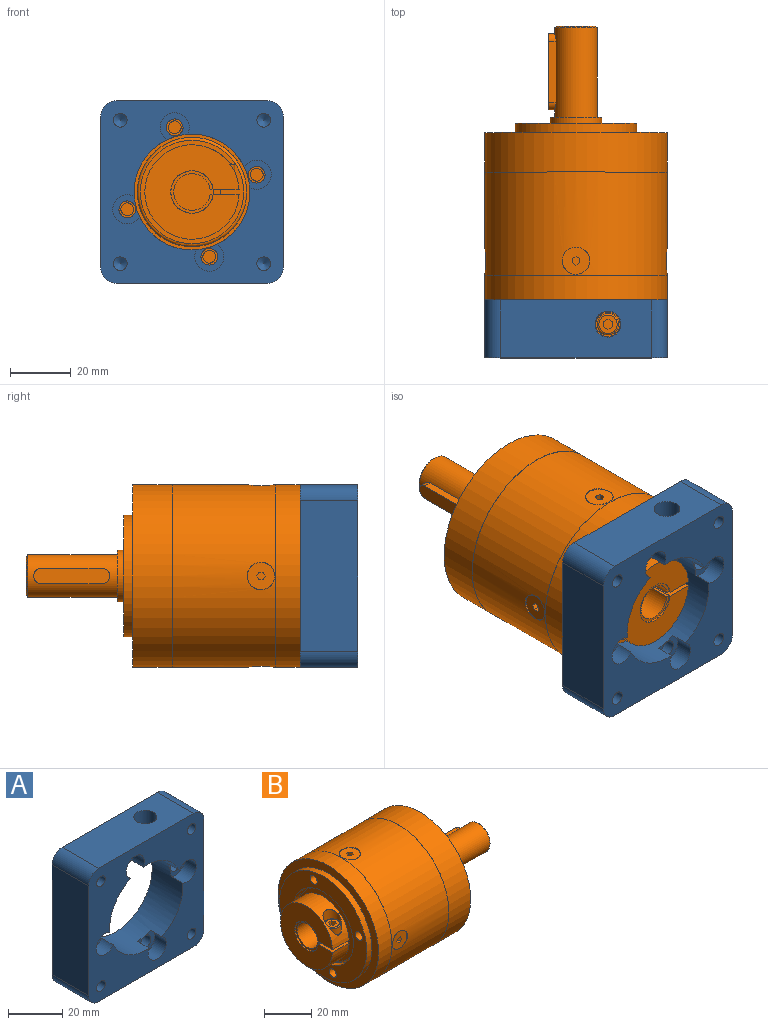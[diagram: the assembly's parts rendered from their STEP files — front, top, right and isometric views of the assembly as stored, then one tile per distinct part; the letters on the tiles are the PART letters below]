
ASSEMBLY  parts=2 mates=1
PART A: 34 faces, bbox 60x19x60 mm
  f0: plane 60x60mm, normal (0,-1,0), area 2122.8mm2, adj f1,f3,f4,f5,f6,f9,f11,f13
  f1: plane 49.4x19mm, normal (0,0,-1), area 938.6mm2, adj f0,f2,f32,f33
  f2: plane 60x60mm, normal (0,1,0), area 1452.2mm2, adj f1,f3,f4,f5,f16,f30,f31,f32
  f3: plane 49.4x19mm, normal (0,0,1), area 881.9mm2, adj f0,f2,f7,f30,f31
  f4: plane 49.4x19mm, normal (1,0,0), area 938.6mm2, adj f0,f2,f31,f32
  f5: plane 49.4x19mm, normal (-1,0,0), area 938.6mm2, adj f0,f2,f30,f33
  f6: cylinder r=19.05mm len=38.1mm, axis (0,-1,0), area 1679mm2, adj f0,f7,f17,f18,f19,f21,f22,f24
  f7: cylinder r=4.25mm len=17.94mm, axis (0,0,1), area 388.1mm2, adj f3,f6
  f8: cone r=0mm half-angle=59deg, axis (0,-1,0), area 18.6mm2, adj f9
  f9: cylinder r=2.25mm len=12mm, axis (0,-1,0), area 169.6mm2, adj f0,f8
  f10: cone r=0mm half-angle=59deg, axis (0,-1,0), area 18.6mm2, adj f11
  f11: cylinder r=2.25mm len=12mm, axis (0,-1,0), area 169.6mm2, adj f0,f10
  f12: cone r=0mm half-angle=59deg, axis (0,-1,0), area 18.6mm2, adj f13
  f13: cylinder r=2.25mm len=12mm, axis (0,-1,0), area 169.6mm2, adj f0,f12
  f14: cone r=0mm half-angle=59deg, axis (0,-1,0), area 18.6mm2, adj f15
  f15: cylinder r=2.25mm len=12mm, axis (0,-1,0), area 169.6mm2, adj f0,f14
  f16: cylinder r=26mm len=52mm, axis (0,1,0), area 490.1mm2, adj f2,f17
  f17: plane 52x52mm, normal (0,1,0), area 888.6mm2, adj f6,f16,f20,f23,f26,f29
  f18: plane 9.5x8.8mm, normal (0,-1,0), area 38.6mm2, adj f6,f19,f20
  f19: cylinder r=4.75mm len=9.5mm, axis (0,-1,0), area 132.7mm2, adj f0,f6,f18
  f20: cylinder r=2.75mm len=10mm, axis (0,-1,0), area 172.8mm2, adj f17,f18
  f21: plane 9.5x8.8mm, normal (0,-1,0), area 38.6mm2, adj f6,f22,f23
  f22: cylinder r=4.75mm len=9.5mm, axis (0,-1,0), area 132.7mm2, adj f0,f6,f21
  f23: cylinder r=2.75mm len=10mm, axis (0,-1,0), area 172.8mm2, adj f17,f21
  f24: plane 9.5x8.8mm, normal (0,-1,0), area 38.6mm2, adj f6,f25,f26
  f25: cylinder r=4.75mm len=9.5mm, axis (0,-1,0), area 132.7mm2, adj f0,f6,f24
  f26: cylinder r=2.75mm len=10mm, axis (0,-1,0), area 172.8mm2, adj f17,f24
  f27: plane 9.5x8.8mm, normal (0,-1,0), area 38.6mm2, adj f6,f28,f29
  f28: cylinder r=4.75mm len=9.5mm, axis (0,-1,0), area 132.7mm2, adj f0,f6,f27
  f29: cylinder r=2.75mm len=10mm, axis (0,-1,0), area 172.8mm2, adj f17,f27
  f30: cylinder r=5.3mm len=19mm, axis (0,-1,0), area 158.2mm2, adj f0,f2,f3,f5
  f31: cylinder r=5.3mm len=19mm, axis (0,-1,0), area 158.2mm2, adj f0,f2,f3,f4
  f32: cylinder r=5.3mm len=19mm, axis (0,-1,0), area 158.2mm2, adj f0,f1,f2,f4
  f33: cylinder r=5.3mm len=19mm, axis (0,-1,0), area 158.2mm2, adj f0,f1,f2,f5
PART B: 109 faces, bbox 103.2x60x60 mm
  f0: cylinder r=2.1mm len=4.5mm, axis (-1,0,0), area 59.4mm2, adj f2,f108
  f1: cylinder r=2.15mm len=8mm, axis (-1,0,0), area 108.1mm2, adj f2,f3
  f2: plane 4.3x4.3mm, normal (1,0,0), area 0.7mm2, adj f0,f1
  f3: cone r=2.65mm half-angle=45deg, axis (1,0,0), area 10.7mm2, adj f1,f4
  f4: cylinder r=2.65mm len=5.3mm, axis (-1,0,0), area 26.6mm2, adj f3,f5
  f5: torus R=8.66mm, axis (1,0,0), area 57.4mm2, adj f4,f6
  f6: plane 13x13mm, normal (1,0,0), area 81.2mm2, adj f5,f9
  f7: plane 25x5mm, normal (0,1,0), area 119.6mm2, adj f8,f10,f11,f12
  f8: plane 20x2.46mm, normal (0,0,-1), area 49.2mm2, adj f7,f10,f12,f13
  f9: cone r=7mm half-angle=45deg, axis (-1,0,0), area 30mm2, adj f6,f13
  f10: cylinder r=2.5mm len=5mm, axis (0,-1,0), area 17.5mm2, adj f7,f8,f11,f13
  f11: plane 20x2.46mm, normal (0,0,1), area 49.2mm2, adj f7,f10,f12,f13
  f12: cylinder r=2.5mm len=5mm, axis (0,-1,0), area 17.5mm2, adj f7,f8,f11,f13
  f13: cylinder r=7mm len=29.5mm, axis (-1,0,0), area 1182.4mm2, adj f8,f9,f10,f11,f12,f14
  f14: plane 17x17mm, normal (1,0,0), area 73mm2, adj f13,f15
  f15: cylinder r=8.5mm len=17mm, axis (-1,0,0), area 106.8mm2, adj f14,f21
  f16: plane 3x1.73mm, normal (0,-1,0), area 5.2mm2, adj f22,f23,f35,f67
  f17: plane 4.2x4.2mm, normal (1,0,0), area 13.9mm2, adj f25
  f18: plane 4.2x4.2mm, normal (1,0,0), area 13.9mm2, adj f26
  f19: plane 4.2x4.2mm, normal (1,0,0), area 13.9mm2, adj f27
  f20: plane 4.2x4.2mm, normal (1,0,0), area 13.9mm2, adj f28
  f21: plane 40x40mm, normal (1,0,0), area 1029.7mm2, adj f15,f29
  f22: plane 3x1.5mm, normal (-0.87,-0.5,0), area 5.2mm2, adj f16,f33,f35,f67
  f23: plane 3x1.5mm, normal (0.87,-0.5,0), area 5.2mm2, adj f16,f34,f35,f67
  f24: plane 2.89x2.5mm, normal (0,0,-1), area 5.4mm2, adj f36,f37,f38,f39,f40,f41
  f25: cylinder r=2.1mm len=8mm, axis (1,0,0), area 105.6mm2, adj f17,f42
  f26: cylinder r=2.1mm len=8mm, axis (1,0,0), area 105.6mm2, adj f18,f42
  f27: cylinder r=2.1mm len=8mm, axis (1,0,0), area 105.6mm2, adj f19,f42
  f28: cylinder r=2.1mm len=8mm, axis (1,0,0), area 105.6mm2, adj f20,f42
  f29: cylinder r=20mm len=40mm, axis (-1,0,0), area 377mm2, adj f21,f42
  f30: plane 2.89x2.5mm, normal (0,1,0), area 5.4mm2, adj f43,f44,f45,f46,f47,f48
  f31: plane 2.89x2.5mm, normal (0,-1,0), area 5.4mm2, adj f49,f50,f51,f52,f53,f54
  f32: plane 2.89x2.5mm, normal (0,0,1), area 5.4mm2, adj f55,f56,f57,f58,f59,f60
  f33: plane 3x1.5mm, normal (-0.87,0.5,0), area 5.2mm2, adj f22,f35,f61,f67
  f34: plane 3x1.5mm, normal (0.87,0.5,0), area 5.2mm2, adj f23,f35,f61,f67
  f35: plane 3.46x3mm, normal (0,0,1), area 7.8mm2, adj f16,f22,f23,f33,f34,f61
  f36: plane 2.5x1.44mm, normal (0,1,0), area 3.6mm2, adj f24,f37,f41,f62
  f37: plane 2.5x1.25mm, normal (0.87,0.5,0), area 3.6mm2, adj f24,f36,f38,f62
  f38: plane 2.5x1.25mm, normal (0.87,-0.5,0), area 3.6mm2, adj f24,f37,f39,f62
  f39: plane 2.5x1.44mm, normal (0,-1,0), area 3.6mm2, adj f24,f38,f40,f62
  f40: plane 2.5x1.25mm, normal (-0.87,-0.5,0), area 3.6mm2, adj f24,f39,f41,f62
  f41: plane 2.5x1.25mm, normal (-0.87,0.5,0), area 3.6mm2, adj f24,f36,f40,f62
  f42: plane 60x60mm, normal (1,0,0), area 1515.4mm2, adj f25,f26,f27,f28,f29,f63
  f43: plane 2.5x1.44mm, normal (0,0,1), area 3.6mm2, adj f30,f44,f48,f64
  f44: plane 2.5x1.25mm, normal (0.87,0,0.5), area 3.6mm2, adj f30,f43,f45,f64
  f45: plane 2.5x1.25mm, normal (0.87,0,-0.5), area 3.6mm2, adj f30,f44,f46,f64
  f46: plane 2.5x1.44mm, normal (0,0,-1), area 3.6mm2, adj f30,f45,f47,f64
  f47: plane 2.5x1.25mm, normal (-0.87,0,-0.5), area 3.6mm2, adj f30,f46,f48,f64
  f48: plane 2.5x1.25mm, normal (-0.87,0,0.5), area 3.6mm2, adj f30,f43,f47,f64
  f49: plane 2.5x1.44mm, normal (0,0,-1), area 3.6mm2, adj f31,f50,f54,f65
  f50: plane 2.5x1.25mm, normal (0.87,0,-0.5), area 3.6mm2, adj f31,f49,f51,f65
  f51: plane 2.5x1.25mm, normal (0.87,0,0.5), area 3.6mm2, adj f31,f50,f52,f65
  f52: plane 2.5x1.44mm, normal (0,0,1), area 3.6mm2, adj f31,f51,f53,f65
  f53: plane 2.5x1.25mm, normal (-0.87,0,0.5), area 3.6mm2, adj f31,f52,f54,f65
  f54: plane 2.5x1.25mm, normal (-0.87,0,-0.5), area 3.6mm2, adj f31,f49,f53,f65
  f55: plane 2.5x1.44mm, normal (0,-1,0), area 3.6mm2, adj f32,f56,f60,f66
  f56: plane 2.5x1.25mm, normal (0.87,-0.5,0), area 3.6mm2, adj f32,f55,f57,f66
  f57: plane 2.5x1.25mm, normal (0.87,0.5,0), area 3.6mm2, adj f32,f56,f58,f66
  f58: plane 2.5x1.44mm, normal (0,1,0), area 3.6mm2, adj f32,f57,f59,f66
  f59: plane 2.5x1.25mm, normal (-0.87,0.5,0), area 3.6mm2, adj f32,f58,f60,f66
  f60: plane 2.5x1.25mm, normal (-0.87,-0.5,0), area 3.6mm2, adj f32,f55,f59,f66
  f61: plane 3x1.73mm, normal (0,1,0), area 5.2mm2, adj f33,f34,f35,f67
  f62: plane 9x9mm, normal (0,0,-1), area 58.2mm2, adj f36,f37,f38,f39,f40,f41,f68
  f63: cylinder r=30mm len=60mm, axis (-1,0,0), area 2450.4mm2, adj f42,f69
  f64: plane 9x9mm, normal (0,1,0), area 58.2mm2, adj f43,f44,f45,f46,f47,f48,f70
  f65: plane 9x9mm, normal (0,-1,0), area 58.2mm2, adj f49,f50,f51,f52,f53,f54,f71
  f66: plane 9x9mm, normal (0,0,1), area 58.2mm2, adj f55,f56,f57,f58,f59,f60,f72
  f67: plane 6x6mm, normal (0,0,1), area 20.5mm2, adj f16,f22,f23,f33,f34,f61,f73
  f68: cylinder r=4.5mm len=9mm, axis (0,0,-1), area 6.5mm2, adj f62,f77
  f69: plane 60x60mm, normal (-1,0,0), area 9.4mm2, adj f63,f77
  f70: cylinder r=4.5mm len=9mm, axis (0,1,0), area 6.5mm2, adj f64,f77
  f71: cylinder r=4.5mm len=9mm, axis (0,-1,0), area 6.5mm2, adj f65,f77
  f72: cylinder r=4.5mm len=9mm, axis (0,0,1), area 6.5mm2, adj f66,f77
  f73: torus R=3mm, axis (0,0,1), area 16.4mm2, adj f67,f78
  f74: plane 19.5x0.96mm, normal (0,0,1), area 18.7mm2, adj f75,f79,f80,f83
  f75: plane 13.9x13.86mm, normal (-1,0,0), area 37.2mm2, adj f74,f76,f79,f80
  f76: plane 19.5x0.96mm, normal (0,0,-1), area 18.7mm2, adj f75,f79,f80,f83
  f77: cylinder r=29.95mm len=59.9mm, axis (1,0,0), area 6142.9mm2, adj f68,f69,f70,f71,f72,f81
  f78: cylinder r=3.5mm len=7mm, axis (0,0,-1), area 77mm2, adj f73,f82
  f79: cylinder r=6mm len=19.5mm, axis (1,0,0), area 705.8mm2, adj f74,f75,f76,f83
  f80: cylinder r=6.95mm len=19.5mm, axis (1,0,0), area 822.2mm2, adj f74,f75,f76,f83
  f81: plane 60x60mm, normal (1,0,0), area 9.4mm2, adj f77,f84
  f82: plane 8x7.99mm, normal (0,0,1), area 11.8mm2, adj f78,f85,f95
  f83: plane 14x14mm, normal (-1,0,0), area 116.7mm2, adj f74,f76,f79,f80,f87
  f84: cylinder r=30mm len=60mm, axis (-1,0,0), area 1508mm2, adj f81,f93
  f85: cylinder r=4mm len=8.57mm, axis (0,0,-1), area 129.5mm2, adj f82,f95
  f86: plane 2.54x1.5mm, normal (-1,0,0), area 3.8mm2, adj f87,f94,f96,f104
  f87: cylinder r=7mm len=20mm, axis (-1,0,0), area 864.6mm2, adj f83,f86,f88,f94,f96
  f88: plane 31x30.98mm, normal (-1,0,0), area 588.1mm2, adj f87,f94,f95,f96
  f89: plane 4.2x4.2mm, normal (-1,0,0), area 13.9mm2, adj f97
  f90: plane 4.2x4.2mm, normal (-1,0,0), area 13.9mm2, adj f98
  f91: plane 4.2x4.2mm, normal (-1,0,0), area 13.9mm2, adj f99
  f92: plane 4.2x4.2mm, normal (-1,0,0), area 13.9mm2, adj f100
  f93: plane 60x60mm, normal (-1,0,0), area 703.7mm2, adj f84,f101
  f94: plane 10x8.52mm, normal (0,0,1), area 85.2mm2, adj f86,f87,f88,f95,f102
  f95: cylinder r=15.5mm len=31mm, axis (-1,0,0), area 885.6mm2, adj f82,f85,f88,f94,f96,f102
  f96: plane 10x8.52mm, normal (0,0,-1), area 85.2mm2, adj f86,f87,f88,f95,f102
  f97: cylinder r=2.1mm len=9mm, axis (1,0,0), area 118.8mm2, adj f89,f103
  f98: cylinder r=2.1mm len=9mm, axis (1,0,0), area 118.8mm2, adj f90,f103
  f99: cylinder r=2.1mm len=9mm, axis (1,0,0), area 118.8mm2, adj f91,f103
  f100: cylinder r=2.1mm len=9mm, axis (1,0,0), area 118.8mm2, adj f92,f103
  f101: cylinder r=26mm len=52mm, axis (-1,0,0), area 490.1mm2, adj f93,f103
  f102: plane 31x30.98mm, normal (1,0,0), area 462.2mm2, adj f94,f95,f96,f104
  f103: plane 52x52mm, normal (-1,0,0), area 1050.4mm2, adj f97,f98,f99,f100,f101,f106
  f104: cylinder r=9.5mm len=19mm, axis (-1,0,0), area 125.3mm2, adj f86,f102,f107
  f105: torus R=17mm, axis (1,0,0), area 174.1mm2, adj f106,f107
  f106: cylinder r=18mm len=36mm, axis (-1,0,0), area 350.6mm2, adj f103,f105
  f107: plane 34x34mm, normal (-1,0,0), area 624.4mm2, adj f104,f105
  f108: cone r=2.1mm half-angle=59deg, axis (1,0,0), area 16.2mm2, adj f0
PLACE A at identity
PLACE B rot(axis=(0,0,1),90deg) t=(0,90,0)mm
MATE fastened B.f97 <-> A.f28  axis (0,1,0) through (-5.69,-3,21.25)mm
